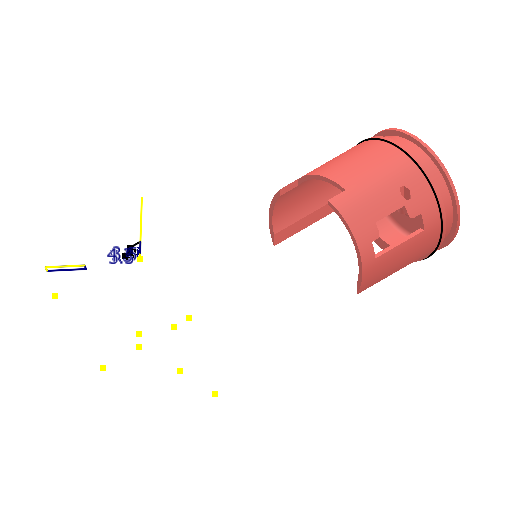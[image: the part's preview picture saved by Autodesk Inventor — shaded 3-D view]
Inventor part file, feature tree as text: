
AUTODESK INVENTOR PART (.ipt)
format: ipt  version: 2025 (Build 290162000, 162)  size: 1,185,280 bytes
history: native  units: in
note: dims shown in document units (in); Inventor stores cm internally (conversion verified against a paired STEP export)
features: sketch x63, extrude x61, fillet x8, plane x6, other x3, direct_edit x2, pattern_circular x2, move_body x2, reference x2, split x1
ambient origin geometry x8: Origin, YZ Plane, XZ Plane, XY Plane, X Axis, Y Axis, Z Axis, Center Point
bodies: Solid1 (feature_tree), Body4 (feature_tree), Solid2 (feature_tree), Solid3 (feature_tree)
feature tree (150):
  direct_edit  "Direct Edit1"
  extrude  "Extrusion1"  Depth=0.2062in TaperAngle=0.0deg
  extrude  "Extrusion2"  Depth=0.1437in TaperAngle=0.0deg
  extrude  "Extrusion3"  Depth=0.0787in TaperAngle=0.0deg
  sketch  "Sketch6"  dims[d11=1.7323in d12=0.9449in]
  extrude  "Extrusion4"  Depth=0.9449in
  extrude  "Extrusion5"  Depth=0.0591in
  pattern_circular  "Circular Pattern1"  Count=9  [1 undecoded]
  extrude  "Extrusion6"  Depth=0.0787in
  extrude  "Extrusion7"  Depth=0.0787in TaperAngle=0.0deg
  pattern_circular  "Circular Pattern2"  Count=9  [1 undecoded]
  fillet  "Fillet1"  Radius=0.1412in
  extrude  "Extrusion8"  Depth=0.063in
  extrude  "Extrusion9"  Depth=0.8312in TaperAngle=0.0deg
  extrude  "Extrusion10"  Depth=0.0787in
  extrude  "Extrusion11"  Depth=0.0787in TaperAngle=0.0deg
  direct_edit  "Direct Edit2"
  extrude  "Extrusion12"  Depth=1.1063in TaperAngle=0.0deg
  extrude  "Extrusion13"  Depth=0.4724in TaperAngle=0.0deg
  extrude  "Extrusion14"  Depth=0.0787in
  extrude  "Extrusion15"  Depth=0.2963in
  extrude  "Extrusion16"  Depth=0.0787in TaperAngle=0.0deg
  extrude  "Extrusion17"  Depth=0.0787in
  fillet  "Fillet2"  Radius=0.0787in
  fillet  "Fillet4"  Radius=0.7338in
  fillet  "Fillet5"  Radius=0.3937in
  extrude  "Extrusion18"  Depth=0.0787in TaperAngle=0.0deg
  extrude  "Extrusion19"  Depth=0.0787in TaperAngle=0.0deg
  extrude  "Extrusion20"  Depth=0.1969in TaperAngle=0.0deg
  fillet  "Fillet6"  Radius=0.1781in
  sketch  "Sketch24"  dims[d72=0.0787in d76=0.1575in d77=0.0in]
  extrude  "Extrusion22"  Depth=1.5438in TaperAngle=0.0deg
  fillet  "Fillet8"  Radius=2.7938in
  extrude  "Extrusion23"  Depth=0.2362in
  extrude  "Extrusion24"  Depth=1.7313in TaperAngle=0.0deg
  extrude  "Extrusion25"  Depth=0.1575in
  sketch  "Sketch30"  dims[d95=0.0709in d96=0.0in d97=0.1575in]
  sketch  "Sketch32"  dims[d98=0.1575in d99=1.6334in d100=0.0in]
  extrude  "Extrusion26"  Depth=1.6334in TaperAngle=0.0deg
  extrude  "Extrusion27"  Depth=0.9459in TaperAngle=0.0deg
  plane  "Work Plane3"
  extrude  "Extrusion28"  Depth=0.0787in TaperAngle=0.0deg
  sketch  "Sketch37"  dims[d116=1.3563in d117=0.0in d118=0.0in]
  extrude  "Extrusion29"  Depth=0.9375in
  extrude  "Extrusion30"  TaperAngle=0.0deg  [1 undecoded]
  extrude  "Extrusion31"  Depth=0.3937in TaperAngle=0.0deg
  extrude  "Extrusion32"  Depth=0.1693in
  sketch  "Sketch42"  dims[d134=0.9173in d135=0.0in d136=4.9173in d137=0.0in]
  extrude  "Extrusion33"  Depth=0.2165in
  sketch  "Sketch44"  dims[d142=4.4562in d143=0.0in d144=0.6063in d145=0.0in]
  sketch  "Sketch45"  dims[d146=0.1378in d147=3.4188in d148=0.0in]
  extrude  "Extrusion34"  Depth=4.9173in TaperAngle=0.0deg
  extrude  "Extrusion35"  Depth=0.9247in TaperAngle=0.0deg
  plane  "Work Plane6"
  plane  "Work Plane7"
  extrude  "Extrusion36"  Depth=0.6063in TaperAngle=0.0deg
  sketch  "Sketch49"  dims[d161=0.2953in d162=0.0in d163=0.2062in d164=0.0in]
  plane  "Work Plane8"
  extrude  "Extrusion37"  Depth=0.1378in TaperAngle=0.0deg
  plane  "Work Plane9"
  split  "Split1"
  move_body  "Move Body1"
  extrude  "Extrusion38"  Depth=0.4813in TaperAngle=0.0deg
  extrude  "Extrusion39"  Depth=0.3937in TaperAngle=0.0deg
  sketch  "Sketch54"  dims[d175=1.6063in d176=0.0in d177=1.811in]
  extrude  "Extrusion40"  Depth=0.2953in TaperAngle=0.0deg
  extrude  "Extrusion41"  Depth=0.2062in TaperAngle=0.0deg
  extrude  "Extrusion42"  Depth=0.0787in
  extrude  "Extrusion43"  Depth=0.0787in TaperAngle=0.0deg
  extrude  "Extrusion44"  Depth=1.9562in TaperAngle=0.0deg
  extrude  "Extrusion45"  Depth=1.811in
  extrude  "Extrusion46"  Depth=0.0591in TaperAngle=0.0deg
  extrude  "Extrusion47"  [1 undecoded]
  sketch  "Sketch56"
  extrude  "Extrusion48"  [1 undecoded]
  extrude  "Extrusion49"  [1 undecoded]
  extrude  "Extrusion50"  [1 undecoded]
  extrude  "Extrusion51"  [1 undecoded]
  extrude  "Extrusion52"  [1 undecoded]
  extrude  "Extrusion53"  [1 undecoded]
  extrude  "Extrusion54"  [1 undecoded]
  extrude  "Extrusion55"  [1 undecoded]
  extrude  "Extrusion56"  [1 undecoded]
  fillet  "Fillet13"  [1 undecoded]
  fillet  "Fillet14"  [1 undecoded]
  extrude  "Extrusion57"  [1 undecoded]
  extrude  "Extrusion58"  [1 undecoded]
  extrude  "Extrusion59"  [1 undecoded]
  extrude  "Extrusion60"  [1 undecoded]
  extrude  "Extrusion61"  [1 undecoded]
  extrude  "Extrusion62"  [1 undecoded]
  sketch  "Sketch1"  dims[d0=0.0in d1=0.0in d2=-0.6875in d3=0.2062in d4=0.0in]
  sketch  "Sketch2"  dims[d5=1.1811in d6=0.1437in d7=0.0in]
  sketch  "Sketch5"  dims[d8=0.0787in d9=1.811in d10=0.0in]
  sketch  "Sketch7"  dims[d13=0.0591in d14=0.0in d15=0.1969in]
  sketch  "Sketch8"  dims[d16=0.1969in]
  sketch  "Sketch9"  dims[d17=0.1841in d18=0.0in d19=3.5433in d20=2.4737in]
  sketch  "Sketch10"  dims[d22=0.0787in d23=0.315in]
  sketch  "Sketch11"  dims[d24=0.0787in d25=1.4409in d26=0.0in]
  sketch  "Sketch12"  dims[d27=1.9966in d28=0.0in d29=3.5433in d30=2.4737in d32=0.1412in]
  sketch  "Sketch13"  dims[d33=0.063in d34=0.063in]
  sketch  "Sketch14"  dims[d35=0.2756in d36=0.0in d37=0.8312in d38=0.0in]
  sketch  "Sketch15"  dims[d39=1.1063in d40=0.0in d41=0.0787in]
  sketch  "Sketch16"  dims[d42=0.0787in d43=0.1688in d44=0.0in]
  sketch  "Sketch17"  dims[d45=0.5187in d46=0.0in d47=1.1063in d48=0.0in]
  sketch  "Sketch18"  dims[d49=1.6535in d50=0.4724in d51=0.0in]
  sketch  "Sketch19"  dims[d52=0.0787in d53=0.0in d54=1.8898in]
  sketch  "Sketch20"  dims[d55=0.2963in d56=0.0in d57=1.2795in]
  sketch  "Sketch21"  dims[d58=1.3583in d59=0.0787in d60=0.0in]
  sketch  "Sketch22"  dims[d61=0.0787in d63=0.0787in d64=0.0787in d65=0.7338in d66=0.0in d67=0.3937in d68=0.0in]
  sketch  "Sketch23"  dims[d69=0.0787in d70=0.8312in d71=0.0in]
  sketch  "Sketch26"  dims[d78=1.3912in d79=0.1969in d80=0.0in d81=0.1781in d82=0.0in]
  sketch  "Sketch27"  dims[d83=0.1575in d84=0.0in d85=1.5438in d86=0.0in d87=2.7938in d88=0.0in]
  sketch  "Sketch28"  dims[d89=1.7313in d90=0.0in d91=0.2362in]
  sketch  "Sketch29"  dims[d92=0.2362in d93=1.7313in d94=0.0in]
  sketch  "Sketch33"  dims[d101=3.5084in d102=0.0in d103=0.9459in d104=0.6917in d105=0.0in d106=0.0in]
  sketch  "Sketch34"  dims[d107=0.1137in d108=0.0in d109=0.0787in d110=0.0in]
  sketch  "Sketch36"  dims[d111=1.6688in d112=0.0in d113=0.9375in]
  reference  "Reference1"
  reference  "Reference2"
  sketch  "Sketch39"  dims[d119=0.0in d120=0.0in d121=-0.3937in d122=0.3937in d123=0.0in]
  sketch  "Sketch40"  dims[d124=1.4562in d125=0.0in d130=0.1693in]
  sketch  "Sketch41"  dims[d131=4.4562in d132=0.0in d133=0.2165in]
  sketch  "Sketch43"  dims[d138=2.6535in d139=0.0in d140=0.9247in d141=0.0in]
  sketch  "Sketch46"  dims[d149=0.2687in d150=0.0in d151=0.4813in d152=0.0in]
  sketch  "Sketch47"  dims[d153=3.5438in d154=0.0in d155=0.3937in d156=0.0in]
  plane  "Work Plane5"
  sketch  "Sketch48"  dims[d157=0.0812in d158=0.0in d159=0.2953in d160=0.0in]
  sketch  "Sketch51"  dims[d165=0.2062in d166=0.0in d167=0.0787in]
  sketch  "Sketch52"  dims[d168=0.0787in d169=1.7313in d170=0.0in]
  sketch  "Sketch53"  dims[d171=4.9562in d172=0.0in d173=1.9562in d174=0.0in]
  sketch  "Sketch55"  dims[d178=0.2938in d179=0.0in d180=0.0591in d181=0.0in]
  sketch  "Sketch57"
  sketch  "Sketch58"
  sketch  "Sketch59"
  sketch  "Sketch60"
  sketch  "Sketch61"
  sketch  "Sketch62"
  sketch  "Sketch63"
  sketch  "Sketch64"
  sketch  "Sketch65"
  sketch  "Sketch66"
  sketch  "Sketch67"
  sketch  "Sketch68"
  sketch  "Sketch69"
  sketch  "Sketch70"
  move_body  "Move1"
  other  "Delete1"
  other  "Full assembly 2.iam"
  other  "main_board:1"
note: 21 required parameter values undecoded (feature->parameter linkage not recoverable at this tier; creation-order binding heuristic only, values carry confidence <= 0.55)
